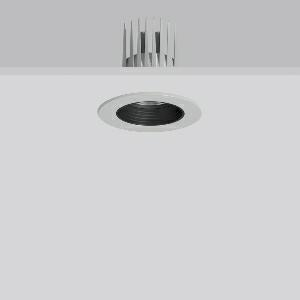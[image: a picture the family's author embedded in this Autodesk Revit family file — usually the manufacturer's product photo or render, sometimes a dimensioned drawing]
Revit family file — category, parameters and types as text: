
# Revit family: heledon_mini_e_901755_004_1_6658
name_source: partatom
category: Lighting Fixtures
units: mm (PartAtom-declared; Revit-internal decimal feet)

## family parameters
Cut with Voids When Loaded = No
Host = Face
Light Source = No
Part Type = Normal
Room Calculation Point = No
Round Connector Dimension = Use Diameter
Shared = No

## types (1)
- HELEDON mini E (1 x LED Modul 940, 2950 lm, 4000)
    Apparent Load = 29 VA
    Approval mark = CE
    CIE Flux Codes = 95 100 100 100 100
    Color Rendering = 92
    Color Temperature = 4000
    Default Elevation = 1800 mm
    Description = Series: HELEDON mini
Round recessed downlight. Housing: die-cast aluminium, powder-coated. Black plastic ring and recessed LED to prevent glare from the side. Optical assembly with lens made of plastic (polycarbonate) for the best homogeneous light distribution - can be changed without tools. Best colour rendering index Ra>90. Suitable for Recessed ceiling mounting. Installation without tools thanks to spring fastening system. Including separate LED converter with connecting cable 600 mm.High quality converter without flickering and stroboscopic effect. Through-wiring box (5 pole) available as accessory. The following accessories can be mounted without use of tools: interchangeable lenses, decorative glasses, honeycomb louvre, clear and frosted diffusers, white interchangeable plastic ring. 
Colour: silver
Diameter: 124 mm
Height: 3 mm
Cut-out diameter: 114 mm
Recess height: 170 mm
Luminaire: recess height: 120 mm
Lamp: LED
Socket: without socket
Colour temperature: 4000K
Colour rendering index (CRI): 92
System power: 29 W
Rated luminous flux: 2950 lm
Luminous efficiency: 102 lm/W
Control gear: Regulated power supply
Protection class: II
Type of protection: IP 20
    Height = 0 mm  [stored 0 ft]
    Lamp = 1 x LED Modul 940
    Lamp Light Flux = 2950 lm
    Lamp count = 1
    Length = 124 mm  [stored 0.406824 ft]
    Lifetime = 50000 h
    Luminous efficacy = 102 lm/W
    Manufacturer = RZB
    ModVariant = No
    Model = 901755.004.1
    Mounting Place = Ceiling
    Mounting Type = Recessed
    Number of Poles = 1
    OnlyDefault = Yes
    Power Factor = 1
    Product Name = HELEDON mini E
    Product group = Recessed downlights
    ProductGroupID = 402
    Protection Class = Protection class II
    Protection Degree = IP 20
    RLX_Detail_Level = 1
    RLX_Emergency_Light_Flux = 0 lm
    RLX_Emergency_Type = 0
    RLX_Emergency_Type_DB = No
    RlxData = <blob elided: 136825 chars, md5=e5ab5c91>
    Socket = socket
    Standby Power = 0 W
    System Light Flux = 2950 lm
    System Power = 29 W
    Type Comments = Product without accessories
    Type Image = 901656.004.jpg
    URL = http://relux.com
    VarID = ---
    Voltage = 230 V
    Voltage Range = 220-240 V
    Weight = 0.00 kg
    Width = 0 mm  [stored 0 ft]

note: [stored X ft] marks values corroborated as IEEE doubles in the binary element streams (Revit-internal decimal feet)

## geometry (parser evidence)
native form markers: Blend x4, Sweep x7
no freeform markers — native parametric forms only
